# Revit family: SKC12R
name_source: partatom
category: Lighting Fixtures
units: mm (PartAtom-declared; Revit-internal decimal feet)

## family parameters
Cut with Voids When Loaded = Yes
Host = Face
Light Source = Yes
Maintain Annotation Orientation = No
Part Type = Normal
Room Calculation Point = No
Round Connector Dimension = Use Diameter
Shared = No

## types (16) — shared parameters
Color Filter = 16777215
Default Elevation = 0' - 0"
Dimming Lamp Color Temperature Shift = <None>
Input Voltage = 120-277V
Lamp = LED
Load Classification = Lighting
Manufacturer = Above All Lighting
Power Factor = 0.9
R = 0' - 6"
Tilt Angle = 90.00°
Trim = 0' - 0 25/32"
URL = https://www.abovealllighting.com
r = 0' - 3 27/32"

## per-type parameters (varying)
| type | CRI | Model | Photometric Web File | Wattage Comments |
| SKC12R-13LM-2700K-CRI90 | 90 | SKC12R-13LM-27901 | SKC12R-13LM27901(G).IES | 15W |
| SKC12R-13LM-3000K-CRI90 | 90 | SKC12R-13LM-30901 | SKC12R-13LM30901(G).IES | 15W |
| SKC12R-13LM-3500K-CRI90 | 90 | SKC12R-13LM-35901 | SKC12R-13LM35901(G).IES | 15W |
| SKC12R-13LM-4000K-CRI90 | 90 | SKC12R-13LM-40901 | SKC12R-13LM40901(G).IES | 15W |
| SKC12R-18LM-2700K-CRI90 | 90 | SKC12R-18LM-27901 | SKC12R-18LM27901(G).IES | 20W |
| SKC12R-18LM-3000K-CRI90 | 90 | SKC12R-18LM-30901 | SKC12R-18LM30901(G).IES | 20W |
| SKC12R-18LM-3500K-CRI90 | 90 | SKC12R-18LM-35901 | SKC12R-18LM35901(G).IES | 20W |
| SKC12R-18LM-4000K-CRI90 | 90 | SKC12R-18LM-40901 | SKC12R-18LM40901(G).IES | 20W |
| SKC12R-13LM-2700K-CRI80 | 80 | SKC12R-13LM-27801 | SKC12R-13LM27801(G).IES | 15W |
| SKC12R-13LM-3000K-CRI80 | 80 | SKC12R-13LM-30801 | SKC12R-13LM30801(G).IES | 15W |
| SKC12R-13LM-3500K-CRI80 | 80 | SKC12R-13LM-35801 | SKC12R-13LM35801(G).IES | 15W |
| SKC12R-13LM-4000K-CRI80 | 80 | SKC12R-13LM-40801 | SKC12R-13LM40801(G).IES | 15W |
| SKC12R-18LM-2700K-CRI80 | 80 | SKC12R-18LM-27801 | SKC12R-18LM27801(G).IES | 20W |
| SKC12R-18LM-3000K-CRI80 | 80 | SKC12R-18LM-30801 | SKC12R-18LM30801(G).IES | 20W |
| SKC12R-18LM-3500K-CRI80 | 80 | SKC12R-18LM-35801 | SKC12R-18LM35801(G).IES | 20W |
| SKC12R-18LM-4000K-CRI80 | 80 | SKC12R-18LM-40801 | SKC12R-18LM40801(G).IES | 20W |

## geometry (parser evidence)
native form markers: Sweep x3
no freeform markers — native parametric forms only
